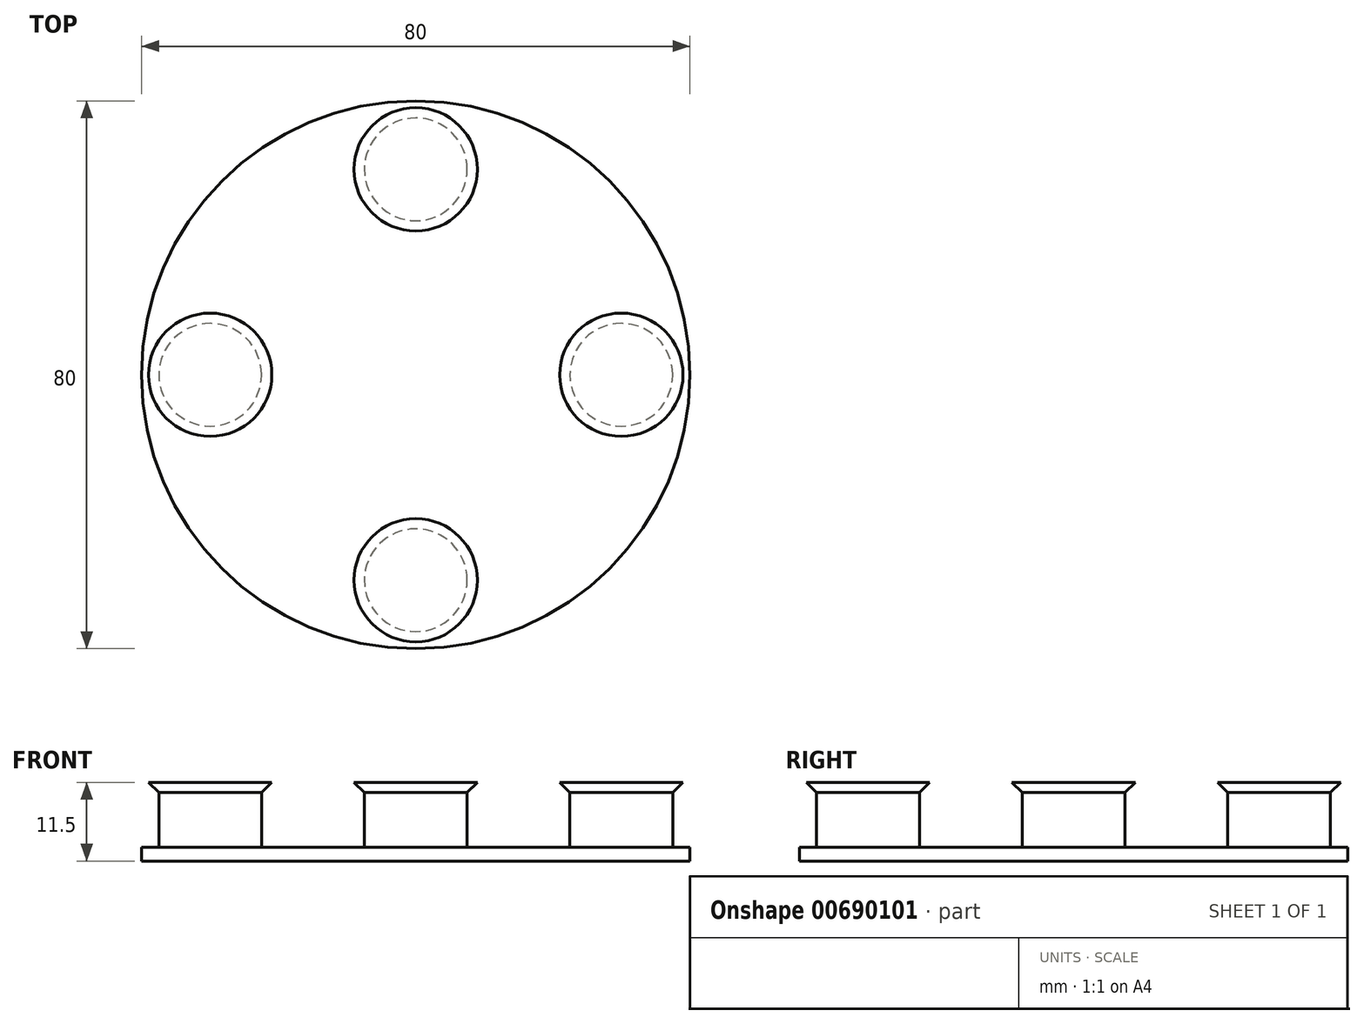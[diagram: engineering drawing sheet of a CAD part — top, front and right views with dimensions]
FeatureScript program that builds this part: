
annotation { "Feature Type Name" : "Feature", "Feature Type Description" : "" }
export const myFeature = defineFeature(function(context is Context, id is Id, definition is map)
    precondition{}
    {
        {
            var Q0;
            Q0=qCreatedBy(makeId("Top.planeOp"),FACE);
            var sketch = newSketch(context, id + "F0", { "sketchPlane" : qUnion([Q0])});
            skCircle(sketch, "E0", {"center": v(0, 0) * mm, "radius": 40 * mm});
            skLineSegment(sketch, "E1", {"start": v(0, 0) * mm, "end": v(0, 30) * mm});
            skCircle(sketch, "E2", {"center": v(0, 30) * mm, "radius": 7.5 * mm});
            skCircle(sketch, "E3.1.0", {"center": v(-30, 0) * mm, "radius": 7.5 * mm});
            skCircle(sketch, "E3.2.0", {"center": v(0, -30) * mm, "radius": 7.5 * mm});
            skCircle(sketch, "E3.3.0", {"center": v(30, 0) * mm, "radius": 7.5 * mm});
            skSolve(sketch);
        }
        {
            var Q0;
            Q0=makeQuery(id+"F0.imprint","IMPRINT",FACE,{"disambiguationData":[TD([[makeQuery(id+"F0.imprint","IMPRINT",EDGE,{"derivedFrom":sQuery(id+"F0.wireOp",EDGE,"E0")}),1.0]])]});
            extrude(context, id + "F1", {"entities" : qUnion([Q0]), "depth" : 2 * mm, "offsetDistance" : 25 * mm});
        }
        {
            var Q0;
            Q0=makeQuery(id+"F0.imprint","IMPRINT",FACE,{"disambiguationData":[TD([[makeQuery(id+"F0.imprint","IMPRINT",EDGE,{"derivedFrom":sQuery(id+"F0.wireOp",EDGE,"E3.2.0")}),1.0]])]});
            var Q1;
            Q1=makeQuery(id+"F0.imprint","IMPRINT",FACE,{"disambiguationData":[TD([[makeQuery(id+"F0.imprint","IMPRINT",EDGE,{"derivedFrom":sQuery(id+"F0.wireOp",EDGE,"E3.3.0")}),1.0]])]});
            var Q2;
            Q2=makeQuery(id+"F0.imprint","IMPRINT",FACE,{"disambiguationData":[TD([[makeQuery(id+"F0.imprint","IMPRINT",EDGE,{"derivedFrom":sQuery(id+"F0.wireOp",EDGE,"E2")}),1.0]])]});
            var Q3;
            Q3=makeQuery(id+"F0.imprint","IMPRINT",FACE,{"disambiguationData":[TD([[makeQuery(id+"F0.imprint","IMPRINT",EDGE,{"derivedFrom":sQuery(id+"F0.wireOp",EDGE,"E3.1.0")}),1.0]])]});
            extrude(context, id + "F2", {"entities" : qUnion([Q0, Q1, Q2, Q3]), "operationType" : NewBodyOperationType.ADD, "depth" : 10 * mm, "offsetDistance" : 25 * mm});
        }
        {
            var Q0;
            Q0=makeQuery(id+"F2.opExtrude","CAP_FACE",FACE,{"disambiguationData":[OSD([sQuery(id+"F0.wireOp",EDGE,"E3.2.0")])],"isStart":false});
            var sketch = newSketch(context, id + "F3", { "sketchPlane" : qUnion([Q0])});
            skCircle(sketch, "E4", {"center": v(0, -30) * mm, "radius": 9 * mm});
            skCircle(sketch, "E5.1.0", {"center": v(30, 0) * mm, "radius": 9 * mm});
            skCircle(sketch, "E5.2.0", {"center": v(0, 30) * mm, "radius": 9 * mm});
            skCircle(sketch, "E5.3.0", {"center": v(-30, 0) * mm, "radius": 9 * mm});
            skPoint(sketch, "E5.center", {"position": v(0, 0) * mm});
            skSolve(sketch);
        }
        {
            var Q0;
            Q0=makeQuery(id+"F3.imprint","IMPRINT",FACE,{"disambiguationData":[TD([[makeQuery(id+"F3.imprint","IMPRINT",EDGE,{"derivedFrom":sQuery(id+"F3.wireOp",EDGE,"E5.3.0")}),1.0]])]});
            var Q1;
            Q1=makeQuery(id+"F3.imprint","IMPRINT",FACE,{"disambiguationData":[TD([[makeQuery(id+"F3.imprint","IMPRINT",EDGE,{"derivedFrom":sQuery(id+"F3.wireOp",EDGE,"E4")}),1.0]])]});
            var Q2;
            Q2=makeQuery(id+"F3.imprint","IMPRINT",FACE,{"disambiguationData":[TD([[makeQuery(id+"F3.imprint","IMPRINT",EDGE,{"derivedFrom":makeQuery(id+"F2.opExtrude","CAP_EDGE",EDGE,{"disambiguationData":[OSD([sQuery(id+"F0.wireOp",EDGE,"E3.2.0")])],"isStart":false})}),1.0]])]});
            var Q3;
            Q3=makeQuery(id+"F3.imprint","IMPRINT",FACE,{"disambiguationData":[TD([[makeQuery(id+"F3.imprint","IMPRINT",EDGE,{"derivedFrom":sQuery(id+"F3.wireOp",EDGE,"E5.1.0")}),1.0]])]});
            var Q4;
            Q4=makeQuery(id+"F3.imprint","IMPRINT",FACE,{"disambiguationData":[TD([[makeQuery(id+"F3.imprint","IMPRINT",EDGE,{"derivedFrom":sQuery(id+"F3.wireOp",EDGE,"E5.2.0")}),1.0]])]});
            extrude(context, id + "F4", {"entities" : qUnion([Q0, Q1, Q2, Q3, Q4]), "operationType" : NewBodyOperationType.ADD, "depth" : 1.5 * mm, "offsetDistance" : 25 * mm});
        }
        {
            var Q0;
            Q0=makeQuery(id+"F4.opExtrude","CAP_EDGE",EDGE,{"disambiguationData":[OSD([sQuery(id+"F3.wireOp",EDGE,"E5.2.0")])],"isStart":true});
            var Q1;
            Q1=makeQuery(id+"F4.opExtrude","CAP_EDGE",EDGE,{"disambiguationData":[OSD([sQuery(id+"F3.wireOp",EDGE,"E5.3.0")])],"isStart":true});
            var Q2;
            Q2=makeQuery(id+"F4.opExtrude","CAP_EDGE",EDGE,{"disambiguationData":[OSD([sQuery(id+"F3.wireOp",EDGE,"E4")])],"isStart":true});
            var Q3;
            Q3=makeQuery(id+"F4.opExtrude","CAP_EDGE",EDGE,{"disambiguationData":[OSD([sQuery(id+"F3.wireOp",EDGE,"E5.1.0")])],"isStart":true});
            chamfer(context, id + "F5", {"entities" : qUnion([Q0, Q1, Q2, Q3]), "width" : 1.5 * mm, "tangentPropagation" : true});
        }
    });
